# Revit family: E-908_RFA
name_source: partatom
category: Aparatos sanitarios
units: mm (PartAtom-declared; Revit-internal decimal feet)

## family parameters
Compartido = No
Corte con vacíos al cargar = No
Cota de conector redondo = Diámetro de uso
Número OmniClass = 23.45.00.00
Punto de cálculo de habitación = No
Se basa en plano de trabajo = No
Siempre vertical = Sí
Tipo de pieza = Normal
Título OmniClass = Sanitary, Laundry, and Cleaning Equipment

## types (1)
- E-908
    Brass Chromed = Brass
    Comentarios de tipo = Single Control Lavatory Faucet
    Data Sheet = http://helvex.com
    Descripción = Explora Single Control Without Drain
    Elevación por defecto = 0"
    Fabricante = HELVEX
    Features = Single Control Ceramic Cartridge; Includes Setting Tools; Flexible Hose 12" Large
    Inlet Threads = ½" - 14 NPT
    Instructive = http://helvex.com
    Max. Working Pressure = 85.3 psi
    Min. Working Pressure = 8.5 psi
    Modelo = E-908
    Total Height = 6"
    Total Length = 6"
    Total Width = 2"
    URL = http://helvex.com

## geometry (parser evidence)
native form markers: Sweep x3
no freeform markers — native parametric forms only
